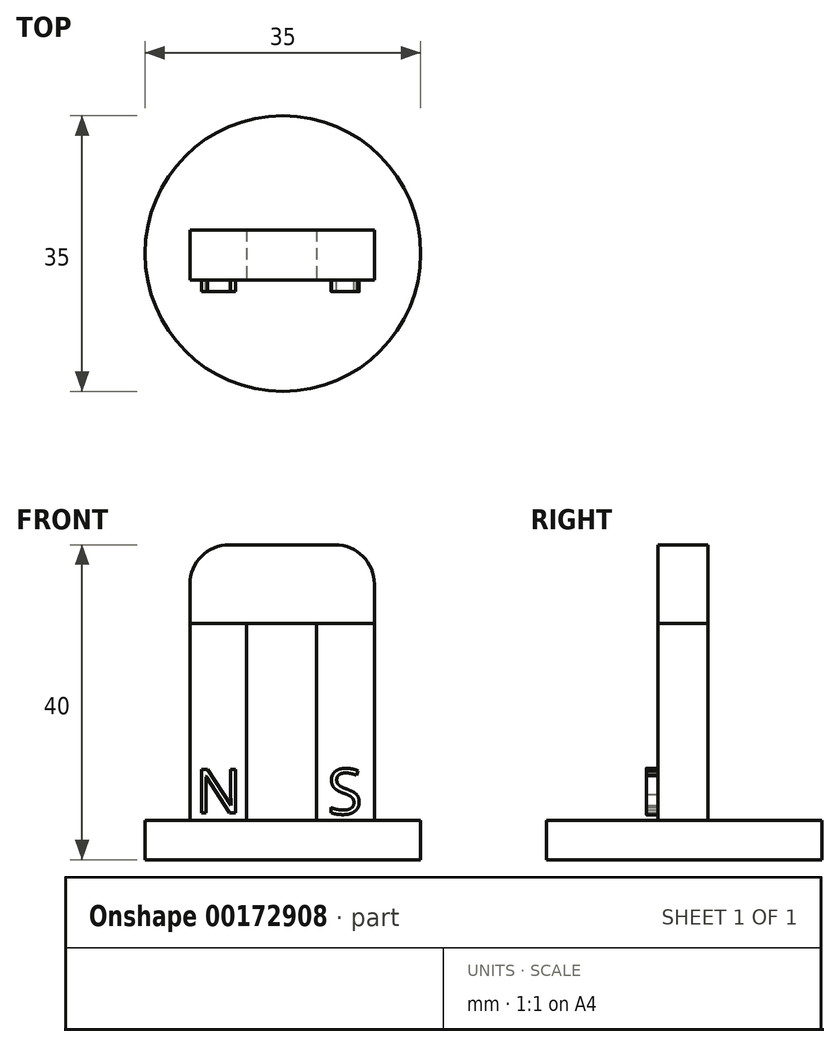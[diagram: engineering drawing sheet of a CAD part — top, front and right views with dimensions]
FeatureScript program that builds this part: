
annotation { "Feature Type Name" : "Feature", "Feature Type Description" : "" }
export const myFeature = defineFeature(function(context is Context, id is Id, definition is map)
    precondition{}
    {
        {
            var Q0;
            Q0=qCreatedBy(makeId("Top.planeOp"),FACE);
            var sketch = newSketch(context, id + "F0", { "sketchPlane" : qUnion([Q0])});
            skCircle(sketch, "E0", {"center": v(0, 0) * mm, "radius": 17.5 * mm});
            skSolve(sketch);
        }
        {
            var Q0;
            Q0 = qSketchRegion(id + "F0", true);
            extrude(context, id + "F1", {"entities" : qUnion([Q0]), "depth" : 5 * mm});
        }
        {
            var Q0;
            Q0=makeQuery(id+"F1.opExtrude","CAP_FACE",FACE,{"disambiguationData":[OSD([sQuery(id+"F0.wireOp",EDGE,"E0")])],"isStart":false});
            var sketch = newSketch(context, id + "F2", { "sketchPlane" : qUnion([Q0])});
            skLineSegment(sketch, "E1.bottom", {"start": v(-11.8, 3.01) * mm, "end": v(-4.63, 3.01) * mm});
            skLineSegment(sketch, "E1.top", {"start": v(-11.8, -3.33) * mm, "end": v(-4.63, -3.33) * mm});
            skLineSegment(sketch, "E1.left", {"start": v(-11.8, 3.01) * mm, "end": v(-11.8, -3.33) * mm});
            skLineSegment(sketch, "E1.right", {"start": v(-4.63, 3.01) * mm, "end": v(-4.63, -3.33) * mm});
            skLineSegment(sketch, "E2.bottom", {"start": v(4.3, 3.01) * mm, "end": v(11.84, 3.01) * mm});
            skLineSegment(sketch, "E2.top", {"start": v(4.3, 3.01) * mm, "end": v(11.84, 3.01) * mm});
            skLineSegment(sketch, "E2.left", {"start": v(4.3, 3.01) * mm, "end": v(4.3, 3.01) * mm});
            skLineSegment(sketch, "E2.right", {"start": v(11.84, 3.01) * mm, "end": v(11.84, 3.01) * mm});
            skLineSegment(sketch, "E3.top", {"start": v(4.3, -3.33) * mm, "end": v(4.3, -3.33) * mm});
            skLineSegment(sketch, "E3.left", {"start": v(4.3, 3.01) * mm, "end": v(4.3, -3.33) * mm});
            skLineSegment(sketch, "E3.right", {"start": v(4.3, 3.01) * mm, "end": v(4.3, -3.33) * mm});
            skLineSegment(sketch, "E4.bottom", {"start": v(4.3, -3.33) * mm, "end": v(11.62, -3.33) * mm});
            skLineSegment(sketch, "E4.top", {"start": v(4.3, -3.33) * mm, "end": v(11.62, -3.33) * mm});
            skLineSegment(sketch, "E4.right", {"start": v(11.62, -3.33) * mm, "end": v(11.62, -3.33) * mm});
            skLineSegment(sketch, "E5.bottom", {"start": v(11.62, 3.01) * mm, "end": v(11.84, 3.01) * mm});
            skLineSegment(sketch, "E5.top", {"start": v(11.62, -3.33) * mm, "end": v(11.84, -3.33) * mm});
            skLineSegment(sketch, "E5.right", {"start": v(11.62, 3.01) * mm, "end": v(11.62, -3.33) * mm});
            skSolve(sketch);
        }
        {
            var Q0;
            Q0 = qSketchRegion(id + "F2", true);
            extrude(context, id + "F3", {"entities" : qUnion([Q0]), "operationType" : NewBodyOperationType.ADD, "depth" : 25 * mm});
        }
        {
            var Q0;
            Q0=makeQuery(id+"F3.opExtrude","CAP_FACE",FACE,{"disambiguationData":[OSD([sQuery(id+"F2.wireOp",EDGE,"E1.bottom"),sQuery(id+"F2.wireOp",EDGE,"E1.top"),sQuery(id+"F2.wireOp",EDGE,"E1.left"),sQuery(id+"F2.wireOp",EDGE,"E1.right")])],"isStart":false});
            var sketch = newSketch(context, id + "F4", { "sketchPlane" : qUnion([Q0])});
            skLineSegment(sketch, "E6.bottom", {"start": v(-11.8, 3.01) * mm, "end": v(11.64, 3.01) * mm});
            skLineSegment(sketch, "E6.top", {"start": v(-11.8, -3.37) * mm, "end": v(11.64, -3.37) * mm});
            skLineSegment(sketch, "E6.left", {"start": v(-11.8, 3.01) * mm, "end": v(-11.8, -3.37) * mm});
            skLineSegment(sketch, "E6.right", {"start": v(11.64, 3.01) * mm, "end": v(11.64, -3.37) * mm});
            skSolve(sketch);
        }
        {
            var Q0;
            Q0 = qSketchRegion(id + "F4", true);
            extrude(context, id + "F5", {"entities" : qUnion([Q0]), "operationType" : NewBodyOperationType.ADD, "depth" : 10 * mm});
        }
        {
            var Q0;
            Q0=makeQuery(id+"F5.opExtrude","CAP_EDGE",EDGE,{"disambiguationData":[OSD([sQuery(id+"F4.wireOp",EDGE,"E6.right")])],"isStart":false});
            var Q1;
            Q1=makeQuery(id+"F5.opExtrude","CAP_EDGE",EDGE,{"disambiguationData":[OSD([sQuery(id+"F4.wireOp",EDGE,"E6.left")])],"isStart":false});
            fillet(context, id + "F6", {"entities" : qUnion([Q0, Q1]), "radius" : 5 * mm, "tangentPropagation" : true, "allowEdgeOverflow" : false});
        }
        {
            var Q0;
            Q0=makeQuery(id+"F3.opExtrude","SWEPT_FACE",FACE,{"disambiguationData":[OSD([sQuery(id+"F2.wireOp",EDGE,"E1.top")])]});
            var sketch = newSketch(context, id + "F7", { "sketchPlane" : qUnion([Q0])});
            skText(sketch, "E7", { "text": "N", "fontName": "OpenSans-Regular.ttf"});
            skText(sketch, "E8", { "text": "S", "fontName": "OpenSans-Regular.ttf"});
            const initialGuessF7  = {"E7": [-0.01107, 0.00597, 1, 0, 0.00555], "E8": [0.00568, 0.0058, 1, 0, 0.00578]};
            skSetInitialGuess(sketch, initialGuessF7);
            skSolve(sketch);
        }
        {
            var Q0;
            Q0 = qSketchRegion(id + "F7", true);
            extrude(context, id + "F8", {"entities" : qUnion([Q0]), "operationType" : NewBodyOperationType.ADD, "depth" : 1.5 * mm});
        }
    });
